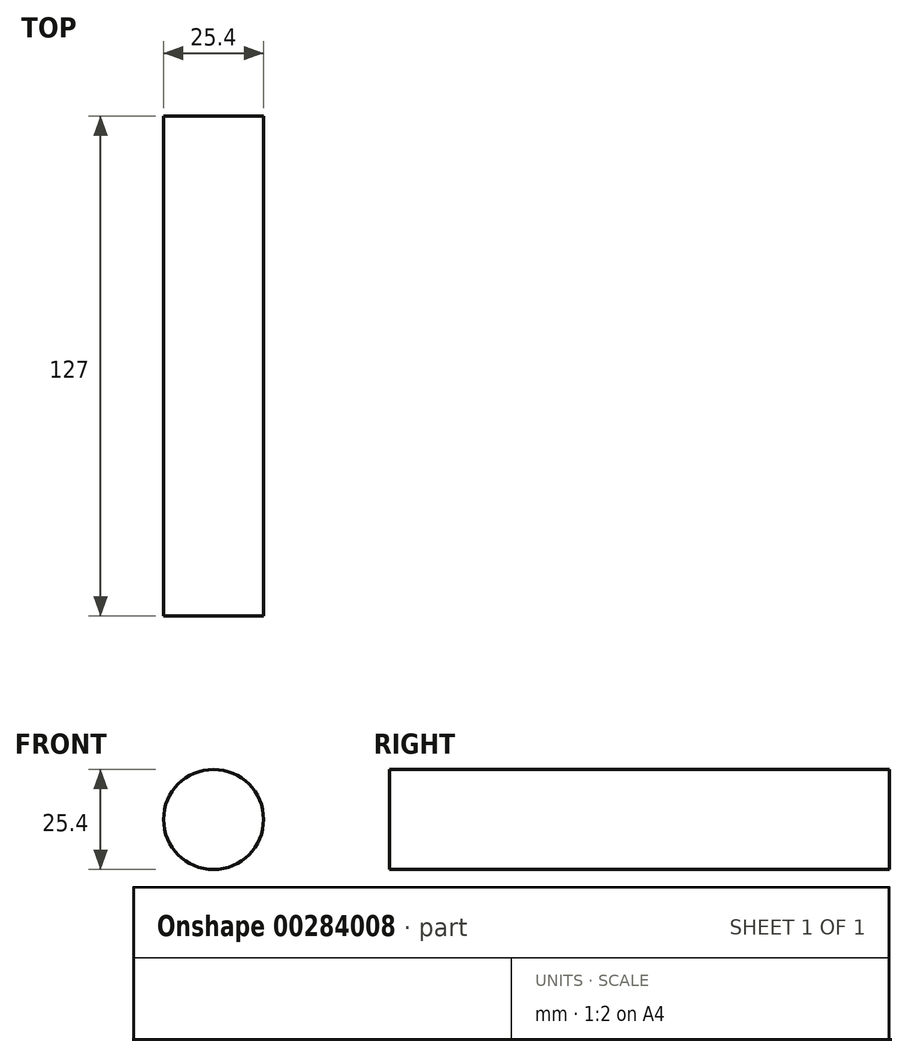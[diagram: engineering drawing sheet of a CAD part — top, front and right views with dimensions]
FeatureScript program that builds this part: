
annotation { "Feature Type Name" : "Feature", "Feature Type Description" : "" }
export const myFeature = defineFeature(function(context is Context, id is Id, definition is map)
    precondition{}
    {
        {
            var Q0;
            Q0=qCreatedBy(makeId("Front.planeOp"),FACE);
            var sketch = newSketch(context, id + "F0", { "sketchPlane" : qUnion([Q0])});
            skCircle(sketch, "E0", {"center": v(-39.72, 27.69) * mm, "radius": 12.7 * mm});
            skSolve(sketch);
        }
        {
            var Q0;
            Q0 = qSketchRegion(id + "F0", true);
            extrude(context, id + "F1", {"entities" : qUnion([Q0]), "depth" : 127 * mm});
        }
    });
